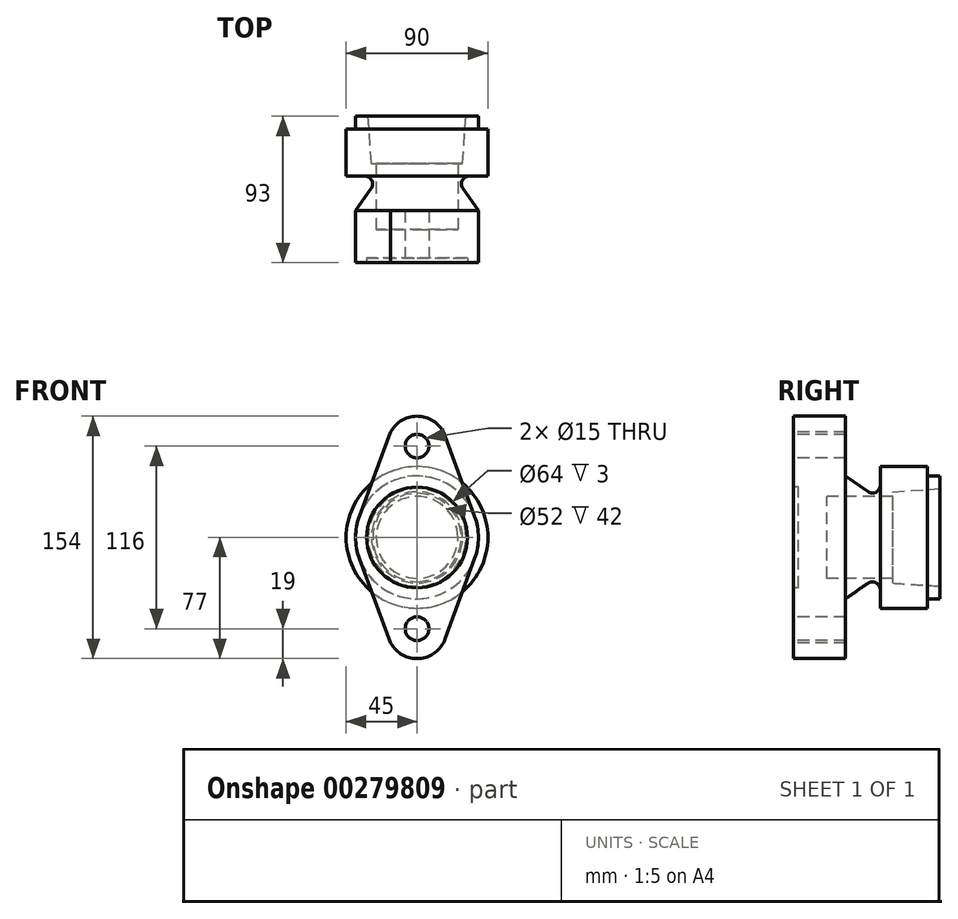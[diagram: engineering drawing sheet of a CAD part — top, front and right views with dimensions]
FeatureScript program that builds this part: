
annotation { "Feature Type Name" : "Feature", "Feature Type Description" : "" }
export const myFeature = defineFeature(function(context is Context, id is Id, definition is map)
    precondition{}
    {
        {
            var Q0;
            Q0=qCreatedBy(makeId("Right.planeOp"),FACE);
            var sketch = newSketch(context, id + "F0", { "sketchPlane" : qUnion([Q0])});
            skLineSegment(sketch, "E0", {"start": v(3, 0) * mm, "end": v(21, 0) * mm});
            skLineSegment(sketch, "E1", {"start": v(21, 0) * mm, "end": v(21, 26) * mm});
            skLineSegment(sketch, "E2", {"start": v(21, 26) * mm, "end": v(63, 26) * mm});
            skLineSegment(sketch, "E3", {"start": v(63, 26) * mm, "end": v(63, 29) * mm});
            skLineSegment(sketch, "E4", {"start": v(63, 29) * mm, "end": v(93, 31) * mm});
            skLineSegment(sketch, "E5", {"start": v(93, 31) * mm, "end": v(93, 39) * mm});
            skLineSegment(sketch, "E6", {"start": v(93, 39) * mm, "end": v(85, 39) * mm});
            skLineSegment(sketch, "E7", {"start": v(85, 39) * mm, "end": v(85, 45) * mm});
            skLineSegment(sketch, "E8", {"start": v(85, 45) * mm, "end": v(55, 45) * mm});
            skLineSegment(sketch, "E9", {"start": v(55, 45) * mm, "end": v(55, 33.2) * mm});
            skPoint(sketch, "E10.end.orphan", {"position": v(36, 45) * mm});
            skLineSegment(sketch, "E11", {"start": v(47.13, 29.1) * mm, "end": v(33, 39) * mm});
            skPoint(sketch, "E12.end.orphan", {"position": v(0, 32) * mm});
            skLineSegment(sketch, "E13", {"start": v(33, 39) * mm, "end": v(0, 39) * mm});
            skPoint(sketch, "E14.start.orphan", {"position": v(4.38, 32) * mm});
            skLineSegment(sketch, "E15", {"start": v(3, 0) * mm, "end": v(3, 32) * mm});
            skLineSegment(sketch, "E16", {"start": v(0, 32) * mm, "end": v(3, 32) * mm});
            skLineSegment(sketch, "E17", {"start": v(0, 39) * mm, "end": v(0, 32) * mm});
            skPoint(sketch, "E18.visualSharp", {"position": v(55, 23.6) * mm});
            skArc(sketch, "E18.filletArc", {"start": v(47.13, 29.1) * mm, "mid": v(52.3, 28.77) * mm, "end": v(55, 33.2) * mm});
            skSolve(sketch);
        }
        {
            var Q0;
            Q0=makeQuery(id+"F0.imprint","IMPRINT",FACE,{"disambiguationData":[TD([[makeQuery(id+"F0.imprint","IMPRINT",EDGE,{"derivedFrom":sQuery(id+"F0.wireOp",EDGE,"E0")}),1.0]])]});
            var Q1;
            Q1=sQuery(id+"F0.wireOp",EDGE,"E0");
            revolve(context, id + "F1", {"entities" : qUnion([Q0]), "axis" : qUnion([Q1]), "revolveType" : RevolveType.FULL});
        }
        {
            var Q0;
            Q0=makeQuery(id+"F1.opRevolve","SWEPT_FACE",FACE,{"disambiguationData":[OSD([sQuery(id+"F0.wireOp",EDGE,"E17")])]});
            var sketch = newSketch(context, id + "F2", { "sketchPlane" : qUnion([Q0])});
            skPoint(sketch, "E19.end.orphan", {"position": v(0, 57.3) * mm});
            skCircle(sketch, "E20", {"center": v(0, 58) * mm, "radius": 7.5 * mm});
            skArc(sketch, "E21", {"start": v(17.83, 64.55) * mm, "mid": v(1.34, 76.95) * mm, "end": v(-16.73, 67) * mm});
            skLineSegment(sketch, "E22", {"start": v(17.83, 64.55) * mm, "end": v(36.6, 13.45) * mm});
            skLineSegment(sketch, "E23", {"start": v(-16.73, 67) * mm, "end": v(-36.56, 13.57) * mm});
            skArc(sketch, "E24", {"start": v(-36.56, 13.57) * mm, "mid": v(-39, 0) * mm, "end": v(-36.56, -13.57) * mm});
            skPoint(sketch, "E25.orphan", {"position": v(62.2, 0) * mm});
            skLineSegment(sketch, "E26.trimOffspring", {"start": v(0, 50.5) * mm, "end": v(0, 58) * mm});
            skLineSegment(sketch, "E27", {"start": v(0, 0) * mm, "end": v(0, 58) * mm, "construction": true});
            skLineSegment(sketch, "E28", {"start": v(-45.6, 0) * mm, "end": v(45.6, 0) * mm, "construction": true});
            skCircle(sketch, "E29.MirrorC", {"center": v(0, 0) * mm, "radius": 39 * mm});
            skLineSegment(sketch, "E30.MirrorCS", {"start": v(-16.73, -67) * mm, "end": v(-36.56, -13.57) * mm});
            skArc(sketch, "E31.MirrorCS", {"start": v(17.83, -64.55) * mm, "mid": v(1.34, -76.95) * mm, "end": v(-16.73, -67) * mm});
            skLineSegment(sketch, "E32.MirrorCS", {"start": v(17.83, -64.55) * mm, "end": v(36.6, -13.45) * mm});
            skCircle(sketch, "E33.MirrorC", {"center": v(0, -58) * mm, "radius": 7.5 * mm});
            skArc(sketch, "E34.trimOffspring", {"start": v(36.6, -13.45) * mm, "mid": v(39, 0) * mm, "end": v(36.6, 13.45) * mm});
            skSolve(sketch);
        }
        {
            var Q0;
            Q0=makeQuery(id+"F2.imprint","IMPRINT",FACE,{"disambiguationData":[TD([[makeQuery(id+"F2.imprint","IMPRINT",EDGE,{"derivedFrom":sQuery(id+"F2.wireOp",EDGE,"E20")}),-1.0]])]});
            var Q1;
            {var subQ1=sQuery(id+"F2.wireOp",EDGE,"E30.MirrorCS");Q1=makeQuery(id+"F2.imprint","IMPRINT",FACE,{"disambiguationData":[TD([[makeQuery(id+"F2.imprint","IMPRINT",EDGE,{"derivedFrom":subQ1}),-1.0]])]});}
            var Q2;
            Q2=makeQuery(id+"F2.imprint","IMPRINT",FACE,{"disambiguationData":[TD([[makeQuery(id+"F2.imprint","IMPRINT",EDGE,{"derivedFrom":makeQuery(id+"F1.opRevolve","SWEPT_EDGE",EDGE,{"disambiguationData":[OSD([sQuery(id+"F0.wireOp",EDGE,"E16"),sQuery(id+"F0.wireOp",EDGE,"E17")])]})}),-1.0]])]});
            extrude(context, id + "F3", {"entities" : qUnion([Q0, Q1, Q2]), "operationType" : NewBodyOperationType.ADD, "oppositeDirection" : true, "depth" : 33 * mm});
        }
    });
